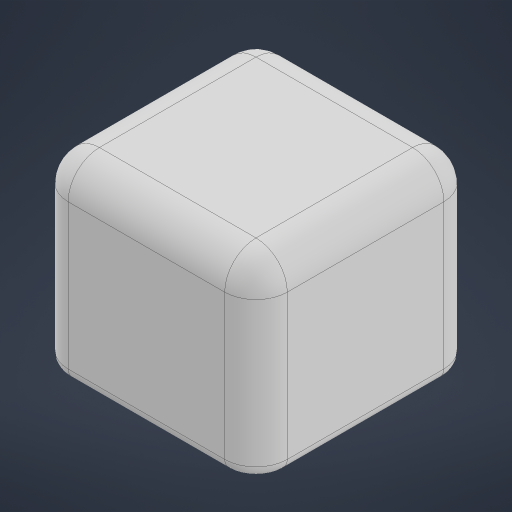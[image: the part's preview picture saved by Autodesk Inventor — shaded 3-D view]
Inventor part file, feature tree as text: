
AUTODESK INVENTOR PART (.ipt)
format: ipt  version: 2024.1 (Build 281209000, 209)  size: 253,952 bytes
history: native  units: mm
features: fillet x4, extrude x2, sketch x2
ambient origin geometry x8: Origin, YZ Plane, XZ Plane, XY Plane, X Axis, Y Axis, Z Axis, Center Point
bodies: Solid1 (feature_tree)
feature tree (8):
  extrude  "Extrusion1"  Depth=20.0mm
  extrude  "Extrusion2"  Depth=1.0mm TaperAngle=0.0deg
  fillet  "Fillet1"  Radius=4.0mm
  fillet  "Fillet2"  Radius=4.0mm
  fillet  "Fillet3"  Radius=1.5mm
  fillet  "Fillet4"  Radius=1.0mm
  sketch  "Sketch1"  dims[d0=20.0mm d1=4.0mm]
  sketch  "Sketch2"  dims[d2=20.0mm d3=0.0mm d4=4.0mm d5=0.0mm d6=4.0mm d7=4.0mm d8=1.5mm d9=1.0mm d10=1.0mm]
